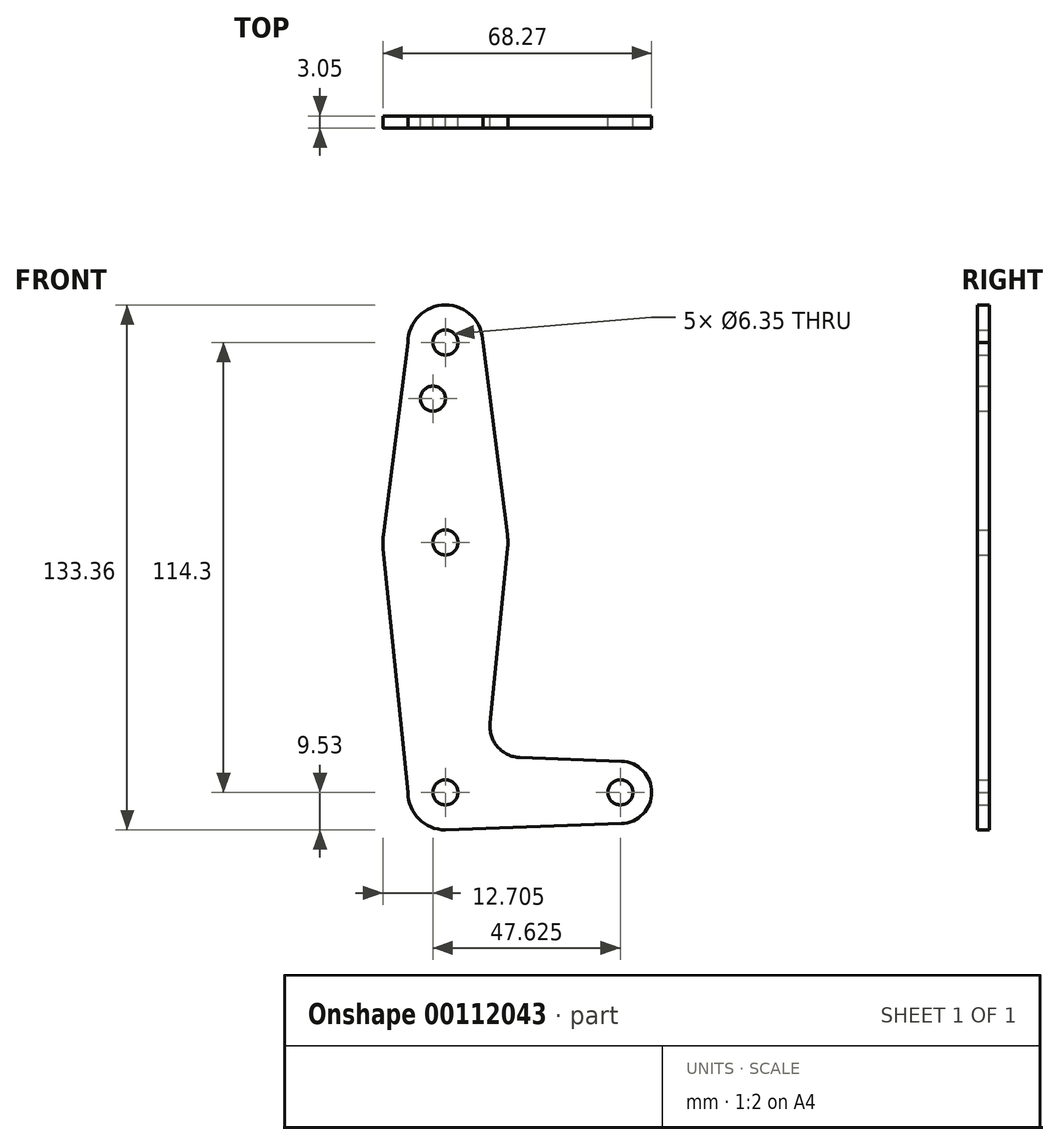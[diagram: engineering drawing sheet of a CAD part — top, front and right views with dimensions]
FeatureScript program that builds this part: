
annotation { "Feature Type Name" : "Feature", "Feature Type Description" : "" }
export const myFeature = defineFeature(function(context is Context, id is Id, definition is map)
    precondition{}
    {
        {
            var Q0;
            Q0=qCreatedBy(makeId("Front.planeOp"),FACE);
            var sketch = newSketch(context, id + "F0", { "sketchPlane" : qUnion([Q0])});
            skLineSegment(sketch, "E0", {"start": v(0, 0) * mm, "end": v(0, 114.3) * mm, "construction": true});
            skLineSegment(sketch, "E1", {"start": v(0, 0) * mm, "end": v(44.45, 0) * mm, "construction": true});
            skCircle(sketch, "E2", {"center": v(0, 114.3) * mm, "radius": 9.53 * mm});
            skCircle(sketch, "E3", {"center": v(0, 0) * mm, "radius": 9.53 * mm});
            skCircle(sketch, "E4", {"center": v(44.45, 0) * mm, "radius": 7.94 * mm});
            skCircle(sketch, "E5", {"center": v(0, 63.5) * mm, "radius": 15.88 * mm});
            skLineSegment(sketch, "E6", {"start": v(-9.52, 114.3) * mm, "end": v(-15.75, 65.5) * mm});
            skLineSegment(sketch, "E7", {"start": v(-15.8, 61.9) * mm, "end": v(-9.52, 0) * mm});
            skLineSegment(sketch, "E8", {"start": v(11.34, 17.6) * mm, "end": v(15.8, 61.91) * mm});
            skLineSegment(sketch, "E9", {"start": v(15.75, 65.5) * mm, "end": v(9.52, 114.3) * mm});
            skLineSegment(sketch, "E10", {"start": v(0, -9.53) * mm, "end": v(44.73, -7.93) * mm});
            skLineSegment(sketch, "E11", {"start": v(18.97, 8.85) * mm, "end": v(44.73, 7.93) * mm});
            skCircle(sketch, "E12", {"center": v(0, 114.3) * mm, "radius": 3.18 * mm});
            skCircle(sketch, "E13", {"center": v(0, 63.5) * mm, "radius": 3.18 * mm});
            skCircle(sketch, "E14", {"center": v(-3.18, 100.03) * mm, "radius": 3.18 * mm});
            skCircle(sketch, "E15", {"center": v(0, 0) * mm, "radius": 3.18 * mm});
            skCircle(sketch, "E16", {"center": v(44.45, 0) * mm, "radius": 3.18 * mm});
            skArc(sketch, "E17.filletArc", {"start": v(11.34, 17.6) * mm, "mid": v(13.26, 11.57) * mm, "end": v(18.97, 8.85) * mm});
            skSolve(sketch);
        }
        {
            var Q0;
            Q0=makeQuery(id+"F0.imprint","IMPRINT",FACE,{"disambiguationData":[TD([[makeQuery(id+"F0.imprint","IMPRINT",EDGE,{"derivedFrom":sQuery(id+"F0.wireOp",EDGE,"E12")}),-1.0]])]});
            var Q1;
            {var subQ1=sQuery(id+"F0.wireOp",EDGE,"E6");Q1=makeQuery(id+"F0.imprint","IMPRINT",FACE,{"disambiguationData":[TD([[makeQuery(id+"F0.imprint","IMPRINT",EDGE,{"derivedFrom":subQ1}),1.0]])]});}
            var Q2;
            Q2=makeQuery(id+"F0.imprint","IMPRINT",FACE,{"disambiguationData":[TD([[makeQuery(id+"F0.imprint","IMPRINT",EDGE,{"derivedFrom":sQuery(id+"F0.wireOp",EDGE,"E13")}),-1.0]])]});
            var Q3;
            {var subQ0=sQuery(id+"F0.wireOp",EDGE,"E7");Q3=makeQuery(id+"F0.imprint","IMPRINT",FACE,{"disambiguationData":[TD([[makeQuery(id+"F0.imprint","IMPRINT",EDGE,{"derivedFrom":subQ0}),1.0]])]});}
            var Q4;
            Q4=makeQuery(id+"F0.imprint","IMPRINT",FACE,{"disambiguationData":[TD([[makeQuery(id+"F0.imprint","IMPRINT",EDGE,{"derivedFrom":sQuery(id+"F0.wireOp",EDGE,"E15")}),-1.0]])]});
            var Q5;
            Q5=makeQuery(id+"F0.imprint","IMPRINT",FACE,{"disambiguationData":[TD([[makeQuery(id+"F0.imprint","IMPRINT",EDGE,{"derivedFrom":sQuery(id+"F0.wireOp",EDGE,"E16")}),-1.0]])]});
            extrude(context, id + "F1", {"entities" : qUnion([Q0, Q1, Q2, Q3, Q4, Q5]), "depth" : 3.05 * mm});
        }
    });
